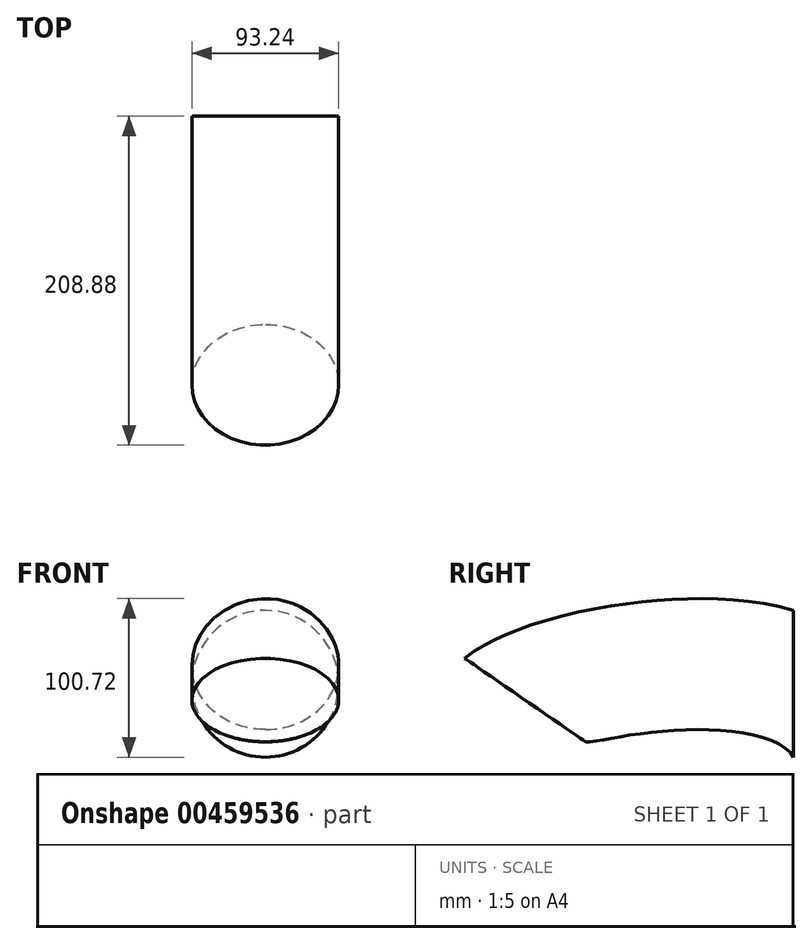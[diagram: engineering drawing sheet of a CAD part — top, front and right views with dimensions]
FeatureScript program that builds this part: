
annotation { "Feature Type Name" : "Feature", "Feature Type Description" : "" }
export const myFeature = defineFeature(function(context is Context, id is Id, definition is map)
    precondition{}
    {
        {
            var Q0;
            Q0=qCreatedBy(makeId("Front.planeOp"),FACE);
            var Q1;
            Q1=qCreatedBy(makeId("Top.planeOp"),FACE);
            cPlane(context, id + "F0", {"entities" : qUnion([Q0, Q1]), "cplaneType" : CPlaneType.MID_PLANE, "offset" : 25.4 * mm, "width" : 152.4 * mm, "height" : 152.4 * mm});
        }
        {
            var Q0;
            Q0=qCreatedBy(makeId("Right.planeOp"),FACE);
            var sketch = newSketch(context, id + "F1", { "sketchPlane" : qUnion([Q0])});
            skFitSpline(sketch, "E0", {"points": [v(0, 0) * mm, v(170.52, 10.32) * mm], "startDerivative": vector(100.54, 54.72) * mm, "endDerivative": vector(135.82, -68.64) * mm});
            skSolve(sketch);
        }
        {
            var Q0;
            Q0=sQuery(id+"F1.wireOp",VERTEX,"E0.1.internal");
            var Q1;
            Q1=qCreatedBy(makeId("Front.planeOp"),FACE);
            cPlane(context, id + "F2", {"entities" : qUnion([Q0, Q1]), "cplaneType" : CPlaneType.PLANE_POINT, "offset" : 25.4 * mm, "width" : 152.4 * mm, "height" : 152.4 * mm});
        }
        {
            var Q0;
            Q0=qCreatedBy(id+"F2.planeOp",FACE);
            var sketch = newSketch(context, id + "F3", { "sketchPlane" : qUnion([Q0])});
            skCircle(sketch, "E1", {"center": v(0, 10.32) * mm, "radius": 46.62 * mm});
            skSolve(sketch);
        }
        {
            var Q0;
            Q0=makeQuery(id+"F3.imprint","IMPRINT",FACE,{"disambiguationData":[TD([[makeQuery(id+"F3.imprint","IMPRINT",EDGE,{"derivedFrom":sQuery(id+"F3.wireOp",EDGE,"E1")}),1.0]])]});
            var Q1;
            Q1=sQuery(id+"F1.wireOp",EDGE,"E0");
            sweep(context, id + "F4", {"profiles" : qUnion([Q0]), "path" : qUnion([Q1])});
        }
    });
